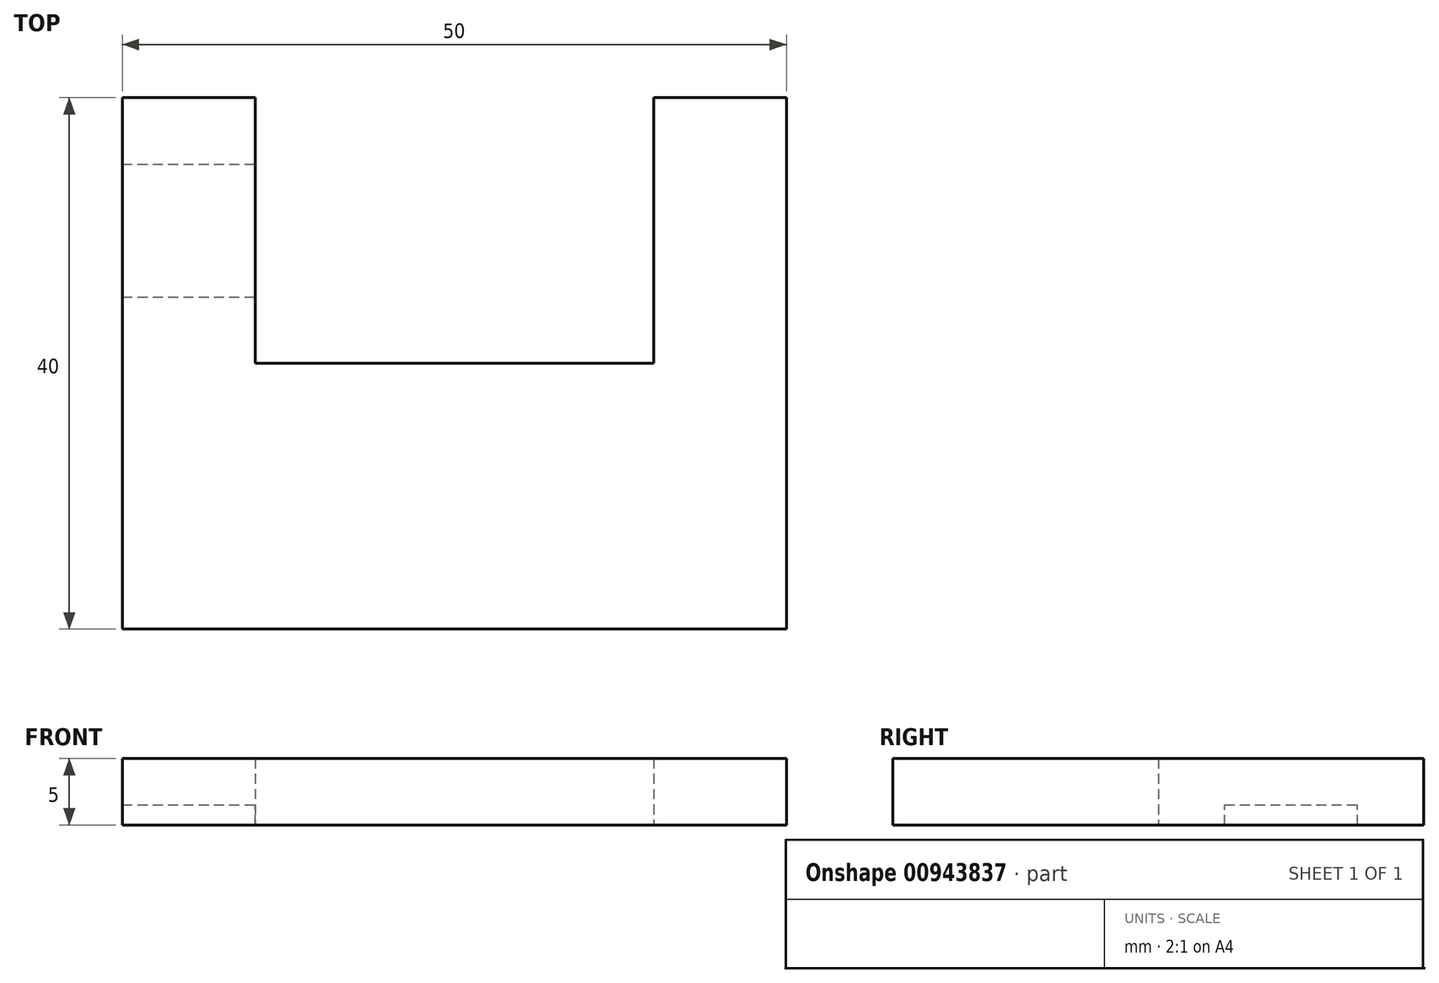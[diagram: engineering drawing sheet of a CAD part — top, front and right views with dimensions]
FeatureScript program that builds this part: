
annotation { "Feature Type Name" : "Feature", "Feature Type Description" : "" }
export const myFeature = defineFeature(function(context is Context, id is Id, definition is map)
    precondition{}
    {
        {
            var Q0;
            Q0=qCreatedBy(makeId("Top.planeOp"),FACE);
            var sketch = newSketch(context, id + "F0", { "sketchPlane" : qUnion([Q0])});
            skLineSegment(sketch, "E0.bottom", {"start": v(25, -20) * mm, "end": v(-25, -20) * mm});
            skLineSegment(sketch, "E0.top", {"start": v(25, 20) * mm, "end": v(15, 20) * mm});
            skLineSegment(sketch, "E0.left", {"start": v(25, -20) * mm, "end": v(25, 20) * mm});
            skLineSegment(sketch, "E0.right", {"start": v(-25, -20) * mm, "end": v(-25, 20) * mm});
            skPoint(sketch, "E0.middle", {"position": v(0, 0) * mm});
            skLineSegment(sketch, "E1.top", {"start": v(15, 0) * mm, "end": v(-15, 0) * mm});
            skLineSegment(sketch, "E1.left", {"start": v(15, 20) * mm, "end": v(15, 0) * mm});
            skLineSegment(sketch, "E1.right", {"start": v(-15, 20) * mm, "end": v(-15, 0) * mm});
            skPoint(sketch, "E1.middle", {"position": v(0, 10) * mm});
            skLineSegment(sketch, "E2.trimOffspring", {"start": v(-15, 20) * mm, "end": v(-25, 20) * mm});
            skSolve(sketch);
        }
        {
            var Q0;
            Q0 = qSketchRegion(id + "F0", true);
            extrude(context, id + "F1", {"entities" : qUnion([Q0]), "depth" : 5 * mm, "offsetDistance" : 25 * mm});
        }
        {
            var Q0;
            Q0=makeQuery(id+"F1.opExtrude","CAP_FACE",FACE,{"disambiguationData":[OSD([sQuery(id+"F0.wireOp",EDGE,"E0.bottom"),sQuery(id+"F0.wireOp",EDGE,"E0.top"),sQuery(id+"F0.wireOp",EDGE,"E0.left"),sQuery(id+"F0.wireOp",EDGE,"E0.right"),sQuery(id+"F0.wireOp",EDGE,"E1.top"),sQuery(id+"F0.wireOp",EDGE,"E1.left"),sQuery(id+"F0.wireOp",EDGE,"E1.right"),sQuery(id+"F0.wireOp",EDGE,"E2.trimOffspring")])],"isStart":true});
            var sketch = newSketch(context, id + "F2", { "sketchPlane" : qUnion([Q0])});
            skLineSegment(sketch, "E3", {"start": v(29.54, -10) * mm, "end": v(-34.72, -10) * mm, "construction": true});
            skLineSegment(sketch, "E4.bottom", {"start": v(-25, -15) * mm, "end": v(-5, -15) * mm});
            skLineSegment(sketch, "E4.top", {"start": v(-25, -5) * mm, "end": v(-5, -5) * mm});
            skLineSegment(sketch, "E4.left", {"start": v(-25, -15) * mm, "end": v(-25, -5) * mm});
            skLineSegment(sketch, "E4.right", {"start": v(-5, -15) * mm, "end": v(-5, -5) * mm});
            skPoint(sketch, "E4.middle", {"position": v(-15, -10) * mm});
            skSolve(sketch);
        }
        {
            var Q0;
            Q0 = qSketchRegion(id + "F2", true);
            extrude(context, id + "F3", {"entities" : qUnion([Q0]), "operationType" : NewBodyOperationType.REMOVE, "oppositeDirection" : true, "depth" : 1.5 * mm, "offsetDistance" : 25 * mm});
        }
    });
